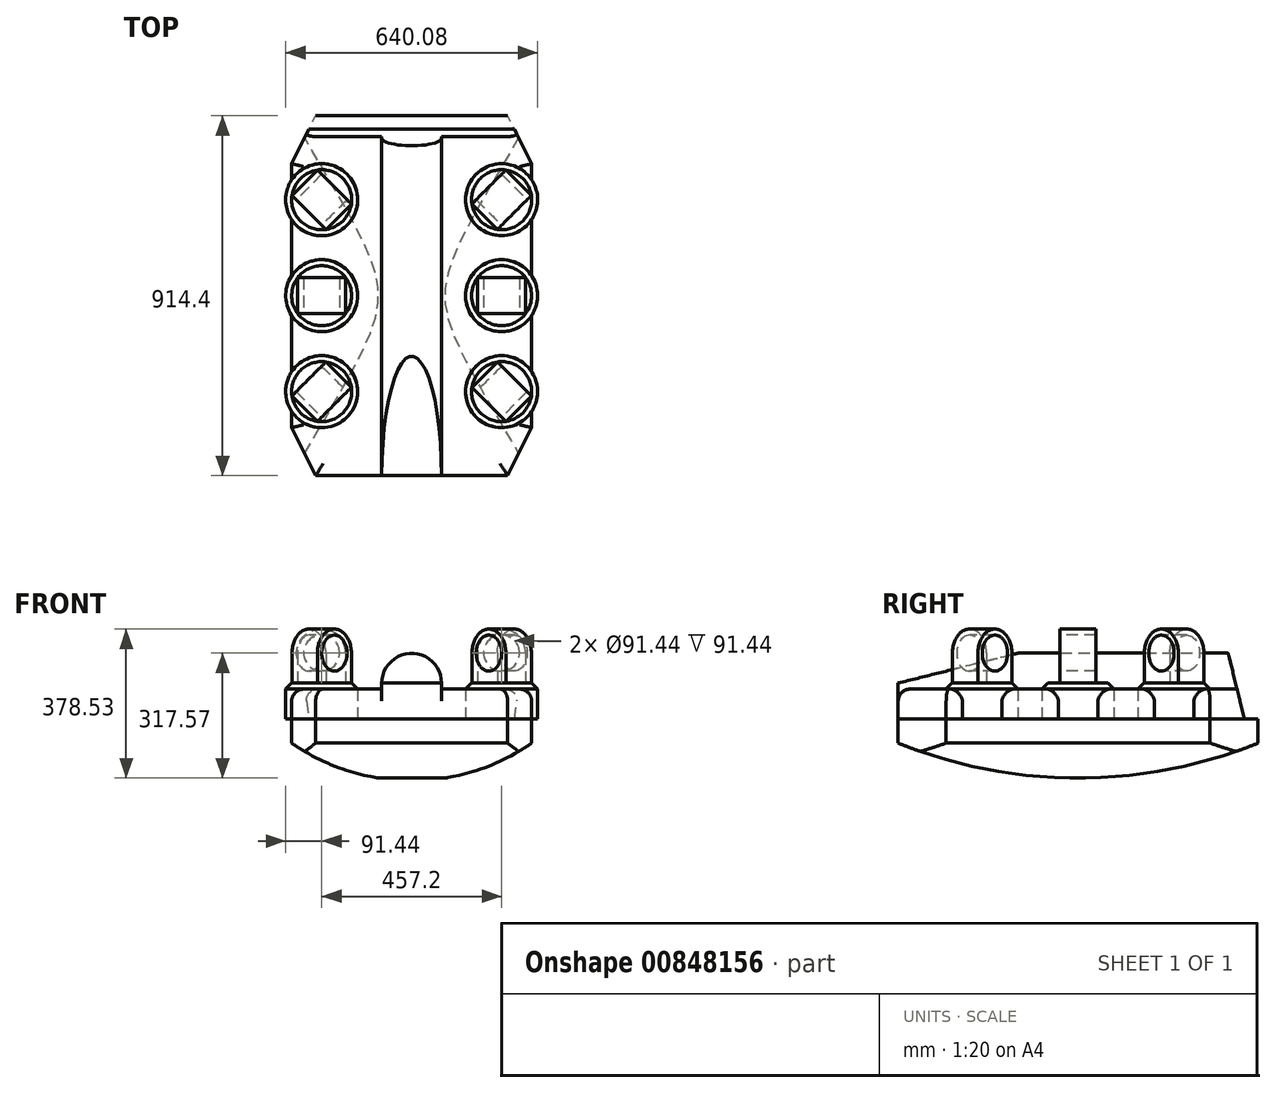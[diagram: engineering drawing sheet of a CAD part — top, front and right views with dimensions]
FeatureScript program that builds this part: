
annotation { "Feature Type Name" : "Feature", "Feature Type Description" : "" }
export const myFeature = defineFeature(function(context is Context, id is Id, definition is map)
    precondition{}
    {
        {
            var Q0;
            Q0=qCreatedBy(makeId("Right.planeOp"),FACE);
            var sketch = newSketch(context, id + "F0", { "sketchPlane" : qUnion([Q0])});
            skLineSegment(sketch, "E0.bottom", {"start": v(-457.2, -30.48) * mm, "end": v(457.2, -30.48) * mm});
            skLineSegment(sketch, "E0.top", {"start": v(-457.2, 30.48) * mm, "end": v(457.2, 30.48) * mm});
            skLineSegment(sketch, "E0.left", {"start": v(-457.2, -30.48) * mm, "end": v(-457.2, 30.48) * mm});
            skLineSegment(sketch, "E0.right", {"start": v(457.2, -30.48) * mm, "end": v(457.2, 30.48) * mm});
            skPoint(sketch, "E0.middle", {"position": v(0, 0) * mm});
            skArc(sketch, "E1", {"start": v(-457.2, -30.48) * mm, "mid": v(0, -119.45) * mm, "end": v(457.2, -30.48) * mm});
            skSolve(sketch);
        }
        {
            var Q0;
            Q0=makeQuery(id+"F0.imprint","IMPRINT",FACE,{"disambiguationData":[TD([[makeQuery(id+"F0.imprint","IMPRINT",EDGE,{"derivedFrom":sQuery(id+"F0.wireOp",EDGE,"E0.bottom")}),1.0]])]});
            var Q1;
            Q1=makeQuery(id+"F0.imprint","IMPRINT",FACE,{"disambiguationData":[TD([[makeQuery(id+"F0.imprint","IMPRINT",EDGE,{"derivedFrom":sQuery(id+"F0.wireOp",EDGE,"E0.bottom")}),-1.0]])]});
            extrude(context, id + "F1", {"entities" : qUnion([Q0, Q1]), "depth" : 609.6 * mm, "offsetDistance" : 30.48 * mm, "symmetric" : true});
        }
        {
            var Q0;
            Q0=qCreatedBy(makeId("Front.planeOp"),FACE);
            var sketch = newSketch(context, id + "F2", { "sketchPlane" : qUnion([Q0])});
            skLineSegment(sketch, "E2.bottom", {"start": v(-304.8, 30.48) * mm, "end": v(304.8, 30.48) * mm});
            skLineSegment(sketch, "E2.top", {"start": v(-304.8, -30.48) * mm, "end": v(304.8, -30.48) * mm});
            skLineSegment(sketch, "E2.left", {"start": v(-304.8, 30.48) * mm, "end": v(-304.8, -30.48) * mm});
            skLineSegment(sketch, "E2.right", {"start": v(304.8, 30.48) * mm, "end": v(304.8, -30.48) * mm});
            skPoint(sketch, "E2.middle", {"position": v(0, 0) * mm});
            skArc(sketch, "E3", {"start": v(-304.8, -30.48) * mm, "mid": v(0, -126.14) * mm, "end": v(304.8, -30.48) * mm});
            skSolve(sketch);
        }
        {
            var Q0;
            Q0 = qSketchRegion(id + "F2", true);
            extrude(context, id + "F3", {"entities" : qUnion([Q0]), "operationType" : NewBodyOperationType.INTERSECT, "depth" : 914.4 * mm, "offsetDistance" : 30.48 * mm, "symmetric" : true});
        }
        {
            var Q0;
            Q0=makeQuery(id+"F1.opExtrude","CAP_EDGE",EDGE,{"disambiguationData":[OSD([sQuery(id+"F0.wireOp",EDGE,"E0.left")])],"isStart":true});
            var Q1;
            Q1=makeQuery(id+"F1.opExtrude","CAP_EDGE",EDGE,{"disambiguationData":[OSD([sQuery(id+"F0.wireOp",EDGE,"E0.left")])],"isStart":false});
            var Q2;
            Q2=makeQuery(id+"F1.opExtrude","CAP_EDGE",EDGE,{"disambiguationData":[OSD([sQuery(id+"F0.wireOp",EDGE,"E0.right")])],"isStart":false});
            var Q3;
            Q3=makeQuery(id+"F1.opExtrude","CAP_EDGE",EDGE,{"disambiguationData":[OSD([sQuery(id+"F0.wireOp",EDGE,"E0.right")])],"isStart":true});
            chamfer(context, id + "F4", {"entities" : qUnion([Q0, Q1, Q2, Q3]), "chamferType" : ChamferType.TWO_OFFSETS, "width1" : 121.92 * mm, "oppositeDirection" : false, "width2" : 60.96 * mm, "tangentPropagation" : true});
        }
        {
            var Q0;
            Q0=makeQuery(id+"F1.opExtrude","SWEPT_FACE",FACE,{"disambiguationData":[OSD([sQuery(id+"F0.wireOp",EDGE,"E0.top")])]});
            var sketch = newSketch(context, id + "F5", { "sketchPlane" : qUnion([Q0])});
            skLineSegment(sketch, "E4.bottom", {"start": v(-228.6, 335.28) * mm, "end": v(228.6, 335.28) * mm});
            skLineSegment(sketch, "E4.top", {"start": v(-228.6, -335.28) * mm, "end": v(228.6, -335.28) * mm});
            skLineSegment(sketch, "E4.left", {"start": v(-228.6, 335.28) * mm, "end": v(-228.6, -335.28) * mm});
            skLineSegment(sketch, "E4.right", {"start": v(228.6, 335.28) * mm, "end": v(228.6, -335.28) * mm});
            skPoint(sketch, "E4.middle", {"position": v(0, 0) * mm});
            skLineSegment(sketch, "E5", {"start": v(-228.6, 243.84) * mm, "end": v(228.6, 243.84) * mm});
            skLineSegment(sketch, "E6", {"start": v(-228.6, 0) * mm, "end": v(228.6, 0) * mm});
            skLineSegment(sketch, "E7", {"start": v(-228.6, -243.84) * mm, "end": v(228.6, -243.84) * mm});
            skCircle(sketch, "E8", {"center": v(-228.6, 243.84) * mm, "radius": 91.44 * mm});
            skCircle(sketch, "E9", {"center": v(-228.6, 0) * mm, "radius": 91.44 * mm});
            skCircle(sketch, "E10", {"center": v(-228.6, -243.84) * mm, "radius": 91.44 * mm});
            skCircle(sketch, "E11", {"center": v(228.6, 243.84) * mm, "radius": 91.44 * mm});
            skCircle(sketch, "E12", {"center": v(228.6, 0) * mm, "radius": 91.44 * mm});
            skCircle(sketch, "E13", {"center": v(228.6, -243.84) * mm, "radius": 91.44 * mm});
            skSolve(sketch);
        }
        {
            var Q0;
            {var subQ1=sQuery(id+"F5.wireOp",EDGE,"E4.left");var subQ7=makeQuery(id+"F5.imprint","INTERSECT",VERTEX,{"derivedFrom":[subQ1,sQuery(id+"F5.wireOp",EDGE,"E5")]});Q0=makeQuery(id+"F5.imprint","IMPRINT",FACE,{"disambiguationData":[TD([[makeQuery(id+"F5.imprint","IMPRINT",EDGE,{"disambiguationData":[TD([[subQ7,-1.0]])],"derivedFrom":subQ1}),-1.0]])]});}
            var Q1;
            {var subQ0=sQuery(id+"F5.wireOp",EDGE,"E5");var subQ1=sQuery(id+"F5.wireOp",EDGE,"E4.left");var subQ2=makeQuery(id+"F5.imprint","INTERSECT",VERTEX,{"derivedFrom":[subQ1,subQ0]});Q1=makeQuery(id+"F5.imprint","IMPRINT",FACE,{"disambiguationData":[TD([[makeQuery(id+"F5.imprint","IMPRINT",EDGE,{"disambiguationData":[TD([[subQ2,-1.0]])],"derivedFrom":subQ1}),1.0]])]});}
            var Q2;
            {var subQ1=sQuery(id+"F5.wireOp",EDGE,"E4.left");var subQ3=sQuery(id+"F5.wireOp",EDGE,"E5");var subQ4=makeQuery(id+"F5.imprint","INTERSECT",VERTEX,{"derivedFrom":[subQ1,subQ3]});Q2=makeQuery(id+"F5.imprint","IMPRINT",FACE,{"disambiguationData":[TD([[makeQuery(id+"F5.imprint","IMPRINT",EDGE,{"disambiguationData":[TD([[subQ4,-1.0]])],"derivedFrom":subQ3}),1.0]])]});}
            var Q3;
            {var subQ0=sQuery(id+"F5.wireOp",EDGE,"E5");var subQ1=sQuery(id+"F5.wireOp",EDGE,"E4.right");var subQ2=makeQuery(id+"F5.imprint","INTERSECT",VERTEX,{"derivedFrom":[subQ1,subQ0]});Q3=makeQuery(id+"F5.imprint","IMPRINT",FACE,{"disambiguationData":[TD([[makeQuery(id+"F5.imprint","IMPRINT",EDGE,{"disambiguationData":[TD([[subQ2,-1.0]])],"derivedFrom":subQ1}),-1.0]])]});}
            var Q4;
            {var subQ1=sQuery(id+"F5.wireOp",EDGE,"E4.right");var subQ3=sQuery(id+"F5.wireOp",EDGE,"E5");var subQ4=makeQuery(id+"F5.imprint","INTERSECT",VERTEX,{"derivedFrom":[subQ1,subQ3]});Q4=makeQuery(id+"F5.imprint","IMPRINT",FACE,{"disambiguationData":[TD([[makeQuery(id+"F5.imprint","IMPRINT",EDGE,{"disambiguationData":[TD([[subQ4,1.0]])],"derivedFrom":subQ3}),1.0]])]});}
            var Q5;
            {var subQ1=sQuery(id+"F5.wireOp",EDGE,"E4.right");var subQ5=makeQuery(id+"F5.imprint","INTERSECT",VERTEX,{"derivedFrom":[subQ1,sQuery(id+"F5.wireOp",EDGE,"E5")]});Q5=makeQuery(id+"F5.imprint","IMPRINT",FACE,{"disambiguationData":[TD([[makeQuery(id+"F5.imprint","IMPRINT",EDGE,{"disambiguationData":[TD([[subQ5,-1.0]])],"derivedFrom":subQ1}),1.0]])]});}
            var Q6;
            {var subQ0=sQuery(id+"F5.wireOp",EDGE,"E6");var subQ1=sQuery(id+"F5.wireOp",EDGE,"E4.right");var subQ2=makeQuery(id+"F5.imprint","INTERSECT",VERTEX,{"derivedFrom":[subQ1,subQ0]});Q6=makeQuery(id+"F5.imprint","IMPRINT",FACE,{"disambiguationData":[TD([[makeQuery(id+"F5.imprint","IMPRINT",EDGE,{"disambiguationData":[TD([[subQ2,1.0]])],"derivedFrom":subQ1}),-1.0]])]});}
            var Q7;
            {var subQ0=sQuery(id+"F5.wireOp",EDGE,"E6");var subQ1=sQuery(id+"F5.wireOp",EDGE,"E4.right");var subQ2=makeQuery(id+"F5.imprint","INTERSECT",VERTEX,{"derivedFrom":[subQ1,subQ0]});Q7=makeQuery(id+"F5.imprint","IMPRINT",FACE,{"disambiguationData":[TD([[makeQuery(id+"F5.imprint","IMPRINT",EDGE,{"disambiguationData":[TD([[subQ2,-1.0]])],"derivedFrom":subQ1}),-1.0]])]});}
            var Q8;
            {var subQ1=sQuery(id+"F5.wireOp",EDGE,"E4.right");var subQ7=makeQuery(id+"F5.imprint","INTERSECT",VERTEX,{"derivedFrom":[subQ1,sQuery(id+"F5.wireOp",EDGE,"E6")]});Q8=makeQuery(id+"F5.imprint","IMPRINT",FACE,{"disambiguationData":[TD([[makeQuery(id+"F5.imprint","IMPRINT",EDGE,{"disambiguationData":[TD([[subQ7,1.0]])],"derivedFrom":subQ1}),1.0]])]});}
            var Q9;
            {var subQ1=sQuery(id+"F5.wireOp",EDGE,"E4.left");var subQ5=makeQuery(id+"F5.imprint","INTERSECT",VERTEX,{"derivedFrom":[subQ1,sQuery(id+"F5.wireOp",EDGE,"E6")]});Q9=makeQuery(id+"F5.imprint","IMPRINT",FACE,{"disambiguationData":[TD([[makeQuery(id+"F5.imprint","IMPRINT",EDGE,{"disambiguationData":[TD([[subQ5,1.0]])],"derivedFrom":subQ1}),-1.0]])]});}
            var Q10;
            {var subQ0=sQuery(id+"F5.wireOp",EDGE,"E6");var subQ1=sQuery(id+"F5.wireOp",EDGE,"E4.left");var subQ2=makeQuery(id+"F5.imprint","INTERSECT",VERTEX,{"derivedFrom":[subQ1,subQ0]});Q10=makeQuery(id+"F5.imprint","IMPRINT",FACE,{"disambiguationData":[TD([[makeQuery(id+"F5.imprint","IMPRINT",EDGE,{"disambiguationData":[TD([[subQ2,-1.0]])],"derivedFrom":subQ1}),1.0]])]});}
            var Q11;
            {var subQ0=sQuery(id+"F5.wireOp",EDGE,"E6");var subQ1=sQuery(id+"F5.wireOp",EDGE,"E4.left");var subQ2=makeQuery(id+"F5.imprint","INTERSECT",VERTEX,{"derivedFrom":[subQ1,subQ0]});Q11=makeQuery(id+"F5.imprint","IMPRINT",FACE,{"disambiguationData":[TD([[makeQuery(id+"F5.imprint","IMPRINT",EDGE,{"disambiguationData":[TD([[subQ2,1.0]])],"derivedFrom":subQ1}),1.0]])]});}
            var Q12;
            {var subQ1=sQuery(id+"F5.wireOp",EDGE,"E4.left");var subQ3=sQuery(id+"F5.wireOp",EDGE,"E7");var subQ4=makeQuery(id+"F5.imprint","INTERSECT",VERTEX,{"derivedFrom":[subQ1,subQ3]});Q12=makeQuery(id+"F5.imprint","IMPRINT",FACE,{"disambiguationData":[TD([[makeQuery(id+"F5.imprint","IMPRINT",EDGE,{"disambiguationData":[TD([[subQ4,-1.0]])],"derivedFrom":subQ3}),-1.0]])]});}
            var Q13;
            {var subQ0=sQuery(id+"F5.wireOp",EDGE,"E7");var subQ1=sQuery(id+"F5.wireOp",EDGE,"E4.left");var subQ2=makeQuery(id+"F5.imprint","INTERSECT",VERTEX,{"derivedFrom":[subQ1,subQ0]});Q13=makeQuery(id+"F5.imprint","IMPRINT",FACE,{"disambiguationData":[TD([[makeQuery(id+"F5.imprint","IMPRINT",EDGE,{"disambiguationData":[TD([[subQ2,1.0]])],"derivedFrom":subQ1}),1.0]])]});}
            var Q14;
            {var subQ1=sQuery(id+"F5.wireOp",EDGE,"E4.left");var subQ5=makeQuery(id+"F5.imprint","INTERSECT",VERTEX,{"derivedFrom":[subQ1,sQuery(id+"F5.wireOp",EDGE,"E7")]});Q14=makeQuery(id+"F5.imprint","IMPRINT",FACE,{"disambiguationData":[TD([[makeQuery(id+"F5.imprint","IMPRINT",EDGE,{"disambiguationData":[TD([[subQ5,1.0]])],"derivedFrom":subQ1}),-1.0]])]});}
            var Q15;
            {var subQ1=sQuery(id+"F5.wireOp",EDGE,"E4.right");var subQ3=sQuery(id+"F5.wireOp",EDGE,"E7");var subQ4=makeQuery(id+"F5.imprint","INTERSECT",VERTEX,{"derivedFrom":[subQ1,subQ3]});Q15=makeQuery(id+"F5.imprint","IMPRINT",FACE,{"disambiguationData":[TD([[makeQuery(id+"F5.imprint","IMPRINT",EDGE,{"disambiguationData":[TD([[subQ4,1.0]])],"derivedFrom":subQ3}),-1.0]])]});}
            var Q16;
            {var subQ0=sQuery(id+"F5.wireOp",EDGE,"E7");var subQ1=sQuery(id+"F5.wireOp",EDGE,"E4.right");var subQ2=makeQuery(id+"F5.imprint","INTERSECT",VERTEX,{"derivedFrom":[subQ1,subQ0]});Q16=makeQuery(id+"F5.imprint","IMPRINT",FACE,{"disambiguationData":[TD([[makeQuery(id+"F5.imprint","IMPRINT",EDGE,{"disambiguationData":[TD([[subQ2,1.0]])],"derivedFrom":subQ1}),-1.0]])]});}
            var Q17;
            {var subQ1=sQuery(id+"F5.wireOp",EDGE,"E4.right");var subQ7=makeQuery(id+"F5.imprint","INTERSECT",VERTEX,{"derivedFrom":[subQ1,sQuery(id+"F5.wireOp",EDGE,"E7")]});Q17=makeQuery(id+"F5.imprint","IMPRINT",FACE,{"disambiguationData":[TD([[makeQuery(id+"F5.imprint","IMPRINT",EDGE,{"disambiguationData":[TD([[subQ7,1.0]])],"derivedFrom":subQ1}),1.0]])]});}
            var Q18;
            {var subQ0=sQuery(id+"F5.wireOp",EDGE,"E13");var subQ1=makeQuery(id+"F1.opExtrude","CAP_EDGE",EDGE,{"disambiguationData":[OSD([sQuery(id+"F0.wireOp",EDGE,"E0.top")])],"isStart":false});var subQ2=makeQuery(id+"F5.imprint","INTERSECT",VERTEX,{"disambiguationData":[OD(0.0)],"derivedFrom":[subQ1,subQ0]});Q18=makeQuery(id+"F5.imprint","IMPRINT",FACE,{"disambiguationData":[TD([[makeQuery(id+"F5.imprint","IMPRINT",EDGE,{"disambiguationData":[TD([[subQ2,1.0]])],"derivedFrom":subQ0}),1.0]])]});}
            var Q19;
            {var subQ0=sQuery(id+"F5.wireOp",EDGE,"E12");var subQ1=makeQuery(id+"F1.opExtrude","CAP_EDGE",EDGE,{"disambiguationData":[OSD([sQuery(id+"F0.wireOp",EDGE,"E0.top")])],"isStart":false});var subQ2=makeQuery(id+"F5.imprint","INTERSECT",VERTEX,{"disambiguationData":[OD(0.0)],"derivedFrom":[subQ1,subQ0]});Q19=makeQuery(id+"F5.imprint","IMPRINT",FACE,{"disambiguationData":[TD([[makeQuery(id+"F5.imprint","IMPRINT",EDGE,{"disambiguationData":[TD([[subQ2,1.0]])],"derivedFrom":subQ0}),1.0]])]});}
            var Q20;
            {var subQ0=sQuery(id+"F5.wireOp",EDGE,"E11");var subQ1=makeQuery(id+"F1.opExtrude","CAP_EDGE",EDGE,{"disambiguationData":[OSD([sQuery(id+"F0.wireOp",EDGE,"E0.top")])],"isStart":false});var subQ2=makeQuery(id+"F5.imprint","INTERSECT",VERTEX,{"disambiguationData":[OD(0.0)],"derivedFrom":[subQ1,subQ0]});Q20=makeQuery(id+"F5.imprint","IMPRINT",FACE,{"disambiguationData":[TD([[makeQuery(id+"F5.imprint","IMPRINT",EDGE,{"disambiguationData":[TD([[subQ2,1.0]])],"derivedFrom":subQ0}),1.0]])]});}
            var Q21;
            {var subQ0=sQuery(id+"F5.wireOp",EDGE,"E8");var subQ1=makeQuery(id+"F1.opExtrude","CAP_EDGE",EDGE,{"disambiguationData":[OSD([sQuery(id+"F0.wireOp",EDGE,"E0.top")])],"isStart":true});var subQ2=makeQuery(id+"F5.imprint","INTERSECT",VERTEX,{"disambiguationData":[OD(0.0)],"derivedFrom":[subQ1,subQ0]});Q21=makeQuery(id+"F5.imprint","IMPRINT",FACE,{"disambiguationData":[TD([[makeQuery(id+"F5.imprint","IMPRINT",EDGE,{"disambiguationData":[TD([[subQ2,-1.0]])],"derivedFrom":subQ0}),1.0]])]});}
            var Q22;
            {var subQ0=sQuery(id+"F5.wireOp",EDGE,"E9");var subQ1=makeQuery(id+"F1.opExtrude","CAP_EDGE",EDGE,{"disambiguationData":[OSD([sQuery(id+"F0.wireOp",EDGE,"E0.top")])],"isStart":true});var subQ2=makeQuery(id+"F5.imprint","INTERSECT",VERTEX,{"disambiguationData":[OD(0.0)],"derivedFrom":[subQ1,subQ0]});Q22=makeQuery(id+"F5.imprint","IMPRINT",FACE,{"disambiguationData":[TD([[makeQuery(id+"F5.imprint","IMPRINT",EDGE,{"disambiguationData":[TD([[subQ2,-1.0]])],"derivedFrom":subQ0}),1.0]])]});}
            var Q23;
            {var subQ0=sQuery(id+"F5.wireOp",EDGE,"E10");var subQ1=makeQuery(id+"F1.opExtrude","CAP_EDGE",EDGE,{"disambiguationData":[OSD([sQuery(id+"F0.wireOp",EDGE,"E0.top")])],"isStart":true});var subQ2=makeQuery(id+"F5.imprint","INTERSECT",VERTEX,{"disambiguationData":[OD(0.0)],"derivedFrom":[subQ1,subQ0]});Q23=makeQuery(id+"F5.imprint","IMPRINT",FACE,{"disambiguationData":[TD([[makeQuery(id+"F5.imprint","IMPRINT",EDGE,{"disambiguationData":[TD([[subQ2,-1.0]])],"derivedFrom":subQ0}),1.0]])]});}
            extrude(context, id + "F6", {"entities" : qUnion([Q0, Q1, Q2, Q3, Q4, Q5, Q6, Q7, Q8, Q9, Q10, Q11, Q12, Q13, Q14, Q15, Q16, Q17, Q18, Q19, Q20, Q21, Q22, Q23]), "operationType" : NewBodyOperationType.ADD, "depth" : 91.44 * mm, "offsetDistance" : 30.48 * mm});
        }
        {
            var Q0;
            Q0=makeQuery(id+"F6.opExtrude","CAP_EDGE",EDGE,{"disambiguationData":[OSD([sQuery(id+"F5.wireOp",EDGE,"E8")])],"isStart":false});
            var Q1;
            Q1=makeQuery(id+"F6.opExtrude","CAP_FACE",FACE,{"disambiguationData":[OSD([sQuery(id+"F5.wireOp",EDGE,"E9")])],"isStart":false});
            var Q2;
            Q2=makeQuery(id+"F6.opExtrude","CAP_FACE",FACE,{"disambiguationData":[OSD([sQuery(id+"F5.wireOp",EDGE,"E10")])],"isStart":false});
            var Q3;
            Q3=makeQuery(id+"F6.opExtrude","CAP_FACE",FACE,{"disambiguationData":[OSD([sQuery(id+"F5.wireOp",EDGE,"E11")])],"isStart":false});
            var Q4;
            Q4=makeQuery(id+"F6.opExtrude","CAP_FACE",FACE,{"disambiguationData":[OSD([sQuery(id+"F5.wireOp",EDGE,"E12")])],"isStart":false});
            var Q5;
            Q5=makeQuery(id+"F6.opExtrude","CAP_FACE",FACE,{"disambiguationData":[OSD([sQuery(id+"F5.wireOp",EDGE,"E13")])],"isStart":false});
            chamfer(context, id + "F7", {"entities" : qUnion([Q0, Q1, Q2, Q3, Q4, Q5]), "width" : 15.24 * mm, "tangentPropagation" : true});
        }
        {
            var Q0;
            Q0=makeQuery(id+"F6.opExtrude","CAP_FACE",FACE,{"disambiguationData":[OSD([sQuery(id+"F5.wireOp",EDGE,"E8")])],"isStart":false});
            var sketch = newSketch(context, id + "F8", { "sketchPlane" : qUnion([Q0])});
            skLineSegment(sketch, "E14.bottom", {"start": v(-250.15, 330.05) * mm, "end": v(-142.39, 222.29) * mm});
            skLineSegment(sketch, "E14.top", {"start": v(-314.81, 265.4) * mm, "end": v(-207.05, 157.63) * mm});
            skLineSegment(sketch, "E14.left", {"start": v(-250.15, 330.05) * mm, "end": v(-314.81, 265.4) * mm});
            skLineSegment(sketch, "E14.right", {"start": v(-142.39, 222.29) * mm, "end": v(-207.05, 157.63) * mm});
            skPoint(sketch, "E14.middle", {"position": v(-228.6, 243.84) * mm});
            skSolve(sketch);
        }
        {
            var Q0;
            {var subQ0=sQuery(id+"F8.wireOp",EDGE,"E14.bottom");var subQ1=sQuery(id+"F5.wireOp",EDGE,"E8");var subQ2=makeQuery(id+"F7.opChamfer","BLEND_EDGE",EDGE,{"blendedFrom":[makeQuery(id+"F6.opExtrude","CAP_EDGE",EDGE,{"disambiguationData":[OSD([subQ1])],"isStart":false}),makeQuery(id+"F6.opExtrude","CAP_FACE",FACE,{"disambiguationData":[OSD([subQ1])],"isStart":false})],"blendedInto":[makeQuery(id+"F6.opExtrude","CAP_FACE",FACE,{"disambiguationData":[OSD([subQ1])],"isStart":false})]});var subQ5=makeQuery(id+"F8.imprint","INTERSECT",VERTEX,{"disambiguationData":[OD(0.0)],"derivedFrom":[subQ2,subQ0]});Q0=makeQuery(id+"F8.imprint","IMPRINT",FACE,{"disambiguationData":[TD([[makeQuery(id+"F8.imprint","IMPRINT",EDGE,{"disambiguationData":[TD([[subQ5,-1.0]])],"derivedFrom":subQ0}),-1.0]])]});}
            extrude(context, id + "F9", {"entities" : qUnion([Q0]), "operationType" : NewBodyOperationType.ADD, "depth" : 152.4 * mm, "offsetDistance" : 30.48 * mm});
        }
        {
            var Q0;
            Q0=makeQuery(id+"F9.opExtrude","SWEPT_FACE",FACE,{"disambiguationData":[OSD([sQuery(id+"F8.wireOp",EDGE,"E14.top")])]});
            var sketch = newSketch(context, id + "F10", { "sketchPlane" : qUnion([Q0])});
            skCircle(sketch, "E15", {"center": v(-334.07, 198.12) * mm, "radius": 45.72 * mm});
            skPoint(sketch, "E15.centerSnap0", {"position": v(-334.07, 274.32) * mm});
            skPoint(sketch, "E15.centerSnap1", {"position": v(-273.1, 198.12) * mm});
            skCircle(sketch, "E16", {"center": v(-334.07, 198.12) * mm, "radius": 60.96 * mm});
            skLineSegment(sketch, "E17.bottom", {"start": v(-410.27, 274.32) * mm, "end": v(-257.87, 274.32) * mm});
            skLineSegment(sketch, "E17.top", {"start": v(-410.27, 121.92) * mm, "end": v(-257.87, 121.92) * mm});
            skLineSegment(sketch, "E17.left", {"start": v(-410.27, 274.32) * mm, "end": v(-410.27, 121.92) * mm});
            skLineSegment(sketch, "E17.right", {"start": v(-257.87, 274.32) * mm, "end": v(-257.87, 121.92) * mm});
            skLineSegment(sketch, "E18", {"start": v(-395.03, 198.12) * mm, "end": v(-395.03, 121.92) * mm});
            skLineSegment(sketch, "E19", {"start": v(-273.1, 198.12) * mm, "end": v(-273.1, 121.92) * mm});
            skSolve(sketch);
        }
        {
            var Q0;
            {var subQ0=sQuery(id+"F10.wireOp",EDGE,"E17.left");Q0=makeQuery(id+"F10.imprint","IMPRINT",FACE,{"disambiguationData":[TD([[makeQuery(id+"F10.imprint","IMPRINT",EDGE,{"derivedFrom":subQ0}),1.0]])]});}
            var Q1;
            {var subQ2=sQuery(id+"F10.wireOp",EDGE,"E17.right");Q1=makeQuery(id+"F10.imprint","IMPRINT",FACE,{"disambiguationData":[TD([[makeQuery(id+"F10.imprint","IMPRINT",EDGE,{"derivedFrom":subQ2}),-1.0]])]});}
            var Q2;
            {var subQ1=sQuery(id+"F8.wireOp",EDGE,"E14.top");var subQ2=sQuery(id+"F5.wireOp",EDGE,"E8");var subQ3=makeQuery(id+"F7.opChamfer","BLEND_EDGE",EDGE,{"blendedFrom":[makeQuery(id+"F6.opExtrude","CAP_EDGE",EDGE,{"disambiguationData":[OSD([subQ2])],"isStart":false}),makeQuery(id+"F6.opExtrude","CAP_FACE",FACE,{"disambiguationData":[OSD([subQ2])],"isStart":false})],"blendedInto":[makeQuery(id+"F6.opExtrude","CAP_FACE",FACE,{"disambiguationData":[OSD([subQ2])],"isStart":false})]});var subQ4=makeQuery(id+"F9.opExtrude","SWEPT_EDGE",EDGE,{"disambiguationData":[OSD([subQ2,subQ1]),TDD([makeQuery(id+"F8.imprint","INTERSECT",VERTEX,{"disambiguationData":[OD(0.0)],"derivedFrom":[subQ3,subQ1]})])]});var subQ8=sQuery(id+"F10.wireOp",EDGE,"E17.bottom");var subQ9=makeQuery(id+"F10.imprint","INTERSECT",VERTEX,{"derivedFrom":[subQ4,subQ8]});Q2=makeQuery(id+"F10.imprint","IMPRINT",FACE,{"disambiguationData":[TD([[makeQuery(id+"F10.imprint","IMPRINT",EDGE,{"disambiguationData":[TD([[subQ9,-1.0]])],"derivedFrom":subQ8}),-1.0]])]});}
            var Q3;
            Q3=makeQuery(id+"F10.imprint","IMPRINT",FACE,{"disambiguationData":[TD([[makeQuery(id+"F10.imprint","IMPRINT",EDGE,{"derivedFrom":sQuery(id+"F10.wireOp",EDGE,"E15")}),1.0]])]});
            extrude(context, id + "F11", {"entities" : qUnion([Q0, Q1, Q2, Q3]), "operationType" : NewBodyOperationType.REMOVE, "oppositeDirection" : true, "depth" : 91.44 * mm, "offsetDistance" : 30.48 * mm});
        }
        {
            var Q0;
            Q0=makeQuery(id+"F6.opExtrude","CAP_FACE",FACE,{"disambiguationData":[OSD([sQuery(id+"F5.wireOp",EDGE,"E9")])],"isStart":false});
            var sketch = newSketch(context, id + "F12", { "sketchPlane" : qUnion([Q0])});
            skLineSegment(sketch, "E20.bottom", {"start": v(-304.8, 45.72) * mm, "end": v(-152.4, 45.72) * mm});
            skLineSegment(sketch, "E20.top", {"start": v(-304.8, -45.72) * mm, "end": v(-152.4, -45.72) * mm});
            skLineSegment(sketch, "E20.left", {"start": v(-304.8, 45.72) * mm, "end": v(-304.8, -45.72) * mm});
            skLineSegment(sketch, "E20.right", {"start": v(-152.4, 45.72) * mm, "end": v(-152.4, -45.72) * mm});
            skPoint(sketch, "E20.middle", {"position": v(-228.6, 0) * mm});
            skSolve(sketch);
        }
        {
            var Q0;
            {var subQ0=sQuery(id+"F12.wireOp",EDGE,"E20.bottom");var subQ1=sQuery(id+"F5.wireOp",EDGE,"E9");var subQ2=makeQuery(id+"F7.opChamfer","BLEND_EDGE",EDGE,{"blendedFrom":[makeQuery(id+"F6.opExtrude","CAP_EDGE",EDGE,{"disambiguationData":[OSD([subQ1])],"isStart":false}),makeQuery(id+"F6.opExtrude","CAP_FACE",FACE,{"disambiguationData":[OSD([subQ1])],"isStart":false})],"blendedInto":[makeQuery(id+"F6.opExtrude","CAP_FACE",FACE,{"disambiguationData":[OSD([subQ1])],"isStart":false})]});var subQ5=makeQuery(id+"F12.imprint","INTERSECT",VERTEX,{"disambiguationData":[OD(0.0)],"derivedFrom":[subQ2,subQ0]});Q0=makeQuery(id+"F12.imprint","IMPRINT",FACE,{"disambiguationData":[TD([[makeQuery(id+"F12.imprint","IMPRINT",EDGE,{"disambiguationData":[TD([[subQ5,-1.0]])],"derivedFrom":subQ0}),-1.0]])]});}
            extrude(context, id + "F13", {"entities" : qUnion([Q0]), "operationType" : NewBodyOperationType.ADD, "depth" : 152.4 * mm, "offsetDistance" : 30.48 * mm});
        }
        {
            var Q0;
            Q0=makeQuery(id+"F13.opExtrude","SWEPT_FACE",FACE,{"disambiguationData":[OSD([sQuery(id+"F12.wireOp",EDGE,"E20.top")])]});
            var sketch = newSketch(context, id + "F14", { "sketchPlane" : qUnion([Q0])});
            skCircle(sketch, "E21", {"center": v(-228.6, 198.12) * mm, "radius": 45.72 * mm});
            skPoint(sketch, "E21.centerSnap0", {"position": v(-228.6, 274.32) * mm});
            skPoint(sketch, "E21.centerSnap1", {"position": v(-167.64, 198.12) * mm});
            skCircle(sketch, "E22", {"center": v(-228.6, 198.12) * mm, "radius": 60.96 * mm});
            skLineSegment(sketch, "E23.bottom", {"start": v(-304.8, 274.32) * mm, "end": v(-152.4, 274.32) * mm});
            skLineSegment(sketch, "E23.top", {"start": v(-304.8, 121.92) * mm, "end": v(-152.4, 121.92) * mm});
            skLineSegment(sketch, "E23.left", {"start": v(-304.8, 274.32) * mm, "end": v(-304.8, 121.92) * mm});
            skLineSegment(sketch, "E23.right", {"start": v(-152.4, 274.32) * mm, "end": v(-152.4, 121.92) * mm});
            skLineSegment(sketch, "E24", {"start": v(-289.56, 198.12) * mm, "end": v(-289.56, 121.92) * mm});
            skLineSegment(sketch, "E25", {"start": v(-167.64, 198.12) * mm, "end": v(-167.64, 121.92) * mm});
            skSolve(sketch);
        }
        {
            var Q0;
            {var subQ5=sQuery(id+"F14.wireOp",EDGE,"E25");Q0=makeQuery(id+"F14.imprint","IMPRINT",FACE,{"disambiguationData":[TD([[makeQuery(id+"F14.imprint","IMPRINT",EDGE,{"derivedFrom":subQ5}),1.0]])]});}
            var Q1;
            {var subQ0=sQuery(id+"F14.wireOp",EDGE,"E23.left");Q1=makeQuery(id+"F14.imprint","IMPRINT",FACE,{"disambiguationData":[TD([[makeQuery(id+"F14.imprint","IMPRINT",EDGE,{"derivedFrom":subQ0}),1.0]])]});}
            var Q2;
            {var subQ4=sQuery(id+"F14.wireOp",EDGE,"E23.right");Q2=makeQuery(id+"F14.imprint","IMPRINT",FACE,{"disambiguationData":[TD([[makeQuery(id+"F14.imprint","IMPRINT",EDGE,{"derivedFrom":subQ4}),-1.0]])]});}
            var Q3;
            Q3=makeQuery(id+"F14.imprint","IMPRINT",FACE,{"disambiguationData":[TD([[makeQuery(id+"F14.imprint","IMPRINT",EDGE,{"derivedFrom":sQuery(id+"F14.wireOp",EDGE,"E21")}),1.0]])]});
            var Q4;
            {var subQ1=sQuery(id+"F12.wireOp",EDGE,"E20.top");var subQ2=sQuery(id+"F5.wireOp",EDGE,"E9");var subQ3=makeQuery(id+"F7.opChamfer","BLEND_EDGE",EDGE,{"blendedFrom":[makeQuery(id+"F6.opExtrude","CAP_EDGE",EDGE,{"disambiguationData":[OSD([subQ2])],"isStart":false}),makeQuery(id+"F6.opExtrude","CAP_FACE",FACE,{"disambiguationData":[OSD([subQ2])],"isStart":false})],"blendedInto":[makeQuery(id+"F6.opExtrude","CAP_FACE",FACE,{"disambiguationData":[OSD([subQ2])],"isStart":false})]});var subQ4=makeQuery(id+"F13.opExtrude","SWEPT_EDGE",EDGE,{"disambiguationData":[OSD([subQ2,subQ1]),TDD([makeQuery(id+"F12.imprint","INTERSECT",VERTEX,{"disambiguationData":[OD(0.0)],"derivedFrom":[subQ3,subQ1]})])]});var subQ8=sQuery(id+"F14.wireOp",EDGE,"E23.bottom");var subQ9=makeQuery(id+"F14.imprint","INTERSECT",VERTEX,{"derivedFrom":[subQ4,subQ8]});Q4=makeQuery(id+"F14.imprint","IMPRINT",FACE,{"disambiguationData":[TD([[makeQuery(id+"F14.imprint","IMPRINT",EDGE,{"disambiguationData":[TD([[subQ9,-1.0]])],"derivedFrom":subQ8}),-1.0]])]});}
            extrude(context, id + "F15", {"entities" : qUnion([Q0, Q1, Q2, Q3, Q4]), "operationType" : NewBodyOperationType.REMOVE, "oppositeDirection" : true, "depth" : 91.44 * mm, "offsetDistance" : 30.48 * mm});
        }
        {
            var Q0;
            Q0=makeQuery(id+"F6.opExtrude","CAP_FACE",FACE,{"disambiguationData":[OSD([sQuery(id+"F5.wireOp",EDGE,"E10")])],"isStart":false});
            var sketch = newSketch(context, id + "F16", { "sketchPlane" : qUnion([Q0])});
            skLineSegment(sketch, "E26.bottom", {"start": v(-314.81, -265.4) * mm, "end": v(-207.05, -157.63) * mm});
            skLineSegment(sketch, "E26.top", {"start": v(-250.15, -330.05) * mm, "end": v(-142.39, -222.29) * mm});
            skLineSegment(sketch, "E26.left", {"start": v(-314.81, -265.4) * mm, "end": v(-250.15, -330.05) * mm});
            skLineSegment(sketch, "E26.right", {"start": v(-207.05, -157.63) * mm, "end": v(-142.39, -222.29) * mm});
            skPoint(sketch, "E26.middle", {"position": v(-228.6, -243.84) * mm});
            skSolve(sketch);
        }
        {
            var Q0;
            {var subQ0=sQuery(id+"F16.wireOp",EDGE,"E26.bottom");var subQ1=sQuery(id+"F5.wireOp",EDGE,"E10");var subQ2=makeQuery(id+"F7.opChamfer","BLEND_EDGE",EDGE,{"blendedFrom":[makeQuery(id+"F6.opExtrude","CAP_EDGE",EDGE,{"disambiguationData":[OSD([subQ1])],"isStart":false}),makeQuery(id+"F6.opExtrude","CAP_FACE",FACE,{"disambiguationData":[OSD([subQ1])],"isStart":false})],"blendedInto":[makeQuery(id+"F6.opExtrude","CAP_FACE",FACE,{"disambiguationData":[OSD([subQ1])],"isStart":false})]});var subQ5=makeQuery(id+"F16.imprint","INTERSECT",VERTEX,{"disambiguationData":[OD(0.0)],"derivedFrom":[subQ2,subQ0]});Q0=makeQuery(id+"F16.imprint","IMPRINT",FACE,{"disambiguationData":[TD([[makeQuery(id+"F16.imprint","IMPRINT",EDGE,{"disambiguationData":[TD([[subQ5,-1.0]])],"derivedFrom":subQ0}),-1.0]])]});}
            extrude(context, id + "F17", {"entities" : qUnion([Q0]), "operationType" : NewBodyOperationType.ADD, "depth" : 152.4 * mm, "offsetDistance" : 30.48 * mm});
        }
        {
            var Q0;
            Q0=makeQuery(id+"F17.opExtrude","SWEPT_FACE",FACE,{"disambiguationData":[OSD([sQuery(id+"F16.wireOp",EDGE,"E26.top")])]});
            var sketch = newSketch(context, id + "F18", { "sketchPlane" : qUnion([Q0])});
            skCircle(sketch, "E27", {"center": v(-334.07, 198.12) * mm, "radius": 45.72 * mm});
            skPoint(sketch, "E27.centerSnap0", {"position": v(-334.07, 274.32) * mm});
            skPoint(sketch, "E27.centerSnap1", {"position": v(-273.1, 198.12) * mm});
            skCircle(sketch, "E28", {"center": v(-334.07, 198.12) * mm, "radius": 60.96 * mm});
            skLineSegment(sketch, "E29.bottom", {"start": v(-410.27, 274.32) * mm, "end": v(-257.87, 274.32) * mm});
            skLineSegment(sketch, "E29.top", {"start": v(-410.27, 121.92) * mm, "end": v(-257.87, 121.92) * mm});
            skLineSegment(sketch, "E29.left", {"start": v(-410.27, 274.32) * mm, "end": v(-410.27, 121.92) * mm});
            skLineSegment(sketch, "E29.right", {"start": v(-257.87, 274.32) * mm, "end": v(-257.87, 121.92) * mm});
            skLineSegment(sketch, "E30", {"start": v(-395.03, 198.12) * mm, "end": v(-395.03, 121.92) * mm});
            skLineSegment(sketch, "E31", {"start": v(-273.1, 198.12) * mm, "end": v(-273.1, 121.92) * mm});
            skSolve(sketch);
        }
        {
            var Q0;
            {var subQ1=sQuery(id+"F16.wireOp",EDGE,"E26.top");var subQ2=sQuery(id+"F5.wireOp",EDGE,"E10");var subQ3=makeQuery(id+"F7.opChamfer","BLEND_EDGE",EDGE,{"blendedFrom":[makeQuery(id+"F6.opExtrude","CAP_EDGE",EDGE,{"disambiguationData":[OSD([subQ2])],"isStart":false}),makeQuery(id+"F6.opExtrude","CAP_FACE",FACE,{"disambiguationData":[OSD([subQ2])],"isStart":false})],"blendedInto":[makeQuery(id+"F6.opExtrude","CAP_FACE",FACE,{"disambiguationData":[OSD([subQ2])],"isStart":false})]});var subQ4=makeQuery(id+"F17.opExtrude","SWEPT_EDGE",EDGE,{"disambiguationData":[OSD([subQ2,subQ1]),TDD([makeQuery(id+"F16.imprint","INTERSECT",VERTEX,{"disambiguationData":[OD(0.0)],"derivedFrom":[subQ3,subQ1]})])]});var subQ8=sQuery(id+"F18.wireOp",EDGE,"E29.bottom");var subQ9=makeQuery(id+"F18.imprint","INTERSECT",VERTEX,{"derivedFrom":[subQ4,subQ8]});Q0=makeQuery(id+"F18.imprint","IMPRINT",FACE,{"disambiguationData":[TD([[makeQuery(id+"F18.imprint","IMPRINT",EDGE,{"disambiguationData":[TD([[subQ9,-1.0]])],"derivedFrom":subQ8}),-1.0]])]});}
            var Q1;
            {var subQ0=sQuery(id+"F18.wireOp",EDGE,"E29.left");Q1=makeQuery(id+"F18.imprint","IMPRINT",FACE,{"disambiguationData":[TD([[makeQuery(id+"F18.imprint","IMPRINT",EDGE,{"derivedFrom":subQ0}),1.0]])]});}
            var Q2;
            {var subQ2=sQuery(id+"F18.wireOp",EDGE,"E29.right");Q2=makeQuery(id+"F18.imprint","IMPRINT",FACE,{"disambiguationData":[TD([[makeQuery(id+"F18.imprint","IMPRINT",EDGE,{"derivedFrom":subQ2}),-1.0]])]});}
            var Q3;
            Q3=makeQuery(id+"F18.imprint","IMPRINT",FACE,{"disambiguationData":[TD([[makeQuery(id+"F18.imprint","IMPRINT",EDGE,{"derivedFrom":sQuery(id+"F18.wireOp",EDGE,"E27")}),1.0]])]});
            extrude(context, id + "F19", {"entities" : qUnion([Q0, Q1, Q2, Q3]), "operationType" : NewBodyOperationType.REMOVE, "oppositeDirection" : true, "depth" : 91.44 * mm, "offsetDistance" : 30.48 * mm});
        }
        {
            var Q0;
            Q0=makeQuery(id+"F1.opExtrude","SWEPT_BODY",BODY,{"disambiguationData":[OSD([sQuery(id+"F0.wireOp",EDGE,"E0.top"),sQuery(id+"F0.wireOp",EDGE,"E0.left"),sQuery(id+"F0.wireOp",EDGE,"E0.right"),sQuery(id+"F0.wireOp",EDGE,"E1")])]});
            var Q1;
            Q1=qCreatedBy(makeId("Right.planeOp"),FACE);
            mirror(context, id + "F20", {"operationType" : NewBodyOperationType.ADD, "entities" : qUnion([Q0]), "mirrorPlane" : qUnion([Q1])});
        }
        {
            var Q0;
            Q0=makeQuery(id+"F1.opExtrude","SWEPT_FACE",FACE,{"disambiguationData":[OSD([sQuery(id+"F0.wireOp",EDGE,"E0.top")])]});
            extrude(context, id + "F21", {"entities" : qUnion([Q0]), "depth" : 76.2 * mm, "offsetDistance" : 30.48 * mm});
        }
        {
            var Q0;
            Q0=makeQuery(id+"F21.opExtrude","CAP_FACE",FACE,{"disambiguationData":[OSD([sQuery(id+"F0.wireOp",EDGE,"E0.top")])],"isStart":false});
            var sketch = newSketch(context, id + "F22", { "sketchPlane" : qUnion([Q0])});
            skLineSegment(sketch, "E32.bottom", {"start": v(-76.2, -457.2) * mm, "end": v(76.2, -457.2) * mm});
            skLineSegment(sketch, "E32.top", {"start": v(-76.2, 457.2) * mm, "end": v(76.2, 457.2) * mm});
            skLineSegment(sketch, "E32.left", {"start": v(-76.2, -457.2) * mm, "end": v(-76.2, 457.2) * mm});
            skLineSegment(sketch, "E32.right", {"start": v(76.2, -457.2) * mm, "end": v(76.2, 457.2) * mm});
            skPoint(sketch, "E32.middle", {"position": v(0, 0) * mm});
            skLineSegment(sketch, "E33.bottom", {"start": v(-76.2, 152.4) * mm, "end": v(76.2, 152.4) * mm});
            skLineSegment(sketch, "E33.top", {"start": v(-76.2, -152.4) * mm, "end": v(76.2, -152.4) * mm});
            skLineSegment(sketch, "E33.left", {"start": v(-76.2, 152.4) * mm, "end": v(-76.2, -152.4) * mm});
            skLineSegment(sketch, "E33.right", {"start": v(76.2, 152.4) * mm, "end": v(76.2, -152.4) * mm});
            skSolve(sketch);
        }
        {
            var Q0;
            Q0=makeQuery(id+"F22.imprint","IMPRINT",FACE,{"disambiguationData":[TD([[makeQuery(id+"F22.imprint","IMPRINT",EDGE,{"derivedFrom":sQuery(id+"F22.wireOp",EDGE,"E33.bottom")}),-1.0]])]});
            var Q1;
            {var subQ0=sQuery(id+"F22.wireOp",EDGE,"E32.top");Q1=makeQuery(id+"F22.imprint","IMPRINT",FACE,{"disambiguationData":[TD([[makeQuery(id+"F22.imprint","IMPRINT",EDGE,{"derivedFrom":subQ0}),1.0]])]});}
            var Q2;
            {var subQ0=sQuery(id+"F22.wireOp",EDGE,"E32.bottom");Q2=makeQuery(id+"F22.imprint","IMPRINT",FACE,{"disambiguationData":[TD([[makeQuery(id+"F22.imprint","IMPRINT",EDGE,{"derivedFrom":subQ0}),-1.0]])]});}
            extrude(context, id + "F23", {"entities" : qUnion([Q0, Q1, Q2]), "operationType" : NewBodyOperationType.ADD, "depth" : 91.44 * mm, "offsetDistance" : 30.48 * mm});
        }
        {
            var Q0;
            Q0=makeQuery(id+"F23.opExtrude","CAP_EDGE",EDGE,{"disambiguationData":[OSD([sQuery(id+"F22.wireOp",EDGE,"E32.bottom")])],"isStart":false});
            var Q1;
            Q1=makeQuery(id+"F23.opExtrude","CAP_EDGE",EDGE,{"disambiguationData":[OSD([sQuery(id+"F22.wireOp",EDGE,"E32.top")])],"isStart":false});
            chamfer(context, id + "F24", {"entities" : qUnion([Q0, Q1]), "chamferType" : ChamferType.TWO_OFFSETS, "width1" : 76.2 * mm, "oppositeDirection" : false, "width2" : 304.8 * mm, "tangentPropagation" : true});
        }
        {
            var Q0;
            Q0=makeQuery(id+"F23.opExtrude","CAP_EDGE",EDGE,{"disambiguationData":[OSD([sQuery(id+"F22.wireOp",EDGE,"E32.left"),sQuery(id+"F22.wireOp",EDGE,"E33.left")])],"isStart":false});
            var Q1;
            Q1=makeQuery(id+"F23.opExtrude","CAP_EDGE",EDGE,{"disambiguationData":[OSD([sQuery(id+"F22.wireOp",EDGE,"E32.right"),sQuery(id+"F22.wireOp",EDGE,"E33.right")])],"isStart":false});
            fillet(context, id + "F25", {"entities" : qUnion([Q0, Q1]), "radius" : 76.2 * mm, "tangentPropagation" : true, "allowEdgeOverflow" : false});
        }
        {
            var Q0;
            {var subQ0=sQuery(id+"F0.wireOp",EDGE,"E0.top");var subQ1=sQuery(id+"F0.wireOp",EDGE,"E0.right");var subQ2=makeQuery(id+"F1.opExtrude","SWEPT_EDGE",EDGE,{"disambiguationData":[OSD([subQ0,subQ1])]});Q0=makeQuery(id+"F23.boolean.opBoolean","SPLIT",EDGE,{"disambiguationData":[TD([makeQuery(id+"F23.opExtrude","SWEPT_FACE",FACE,{"disambiguationData":[OSD([sQuery(id+"F22.wireOp",EDGE,"E32.right"),sQuery(id+"F22.wireOp",EDGE,"E33.right")])]})])],"derivedFrom":makeQuery(id+"F21.opExtrude","CAP_EDGE",EDGE,{"disambiguationData":[OSD([subQ0,subQ1]),TDD([subQ2])],"isStart":false})});}
            var Q1;
            {var subQ0=sQuery(id+"F0.wireOp",EDGE,"E0.top");var subQ1=sQuery(id+"F0.wireOp",EDGE,"E0.right");Q1=makeQuery(id+"F21.opExtrude","CAP_EDGE",EDGE,{"disambiguationData":[OSD([subQ0,subQ1]),TDD([makeQuery(id+"F4.opChamfer","BLEND_EDGE",EDGE,{"blendedFrom":[makeQuery(id+"F1.opExtrude","CAP_EDGE",EDGE,{"disambiguationData":[OSD([subQ1])],"isStart":false}),makeQuery(id+"F1.opExtrude","SWEPT_FACE",FACE,{"disambiguationData":[OSD([subQ0])]})],"blendedInto":[makeQuery(id+"F1.opExtrude","SWEPT_FACE",FACE,{"disambiguationData":[OSD([subQ0])]})]})])],"isStart":false});}
            var Q2;
            {var subQ0=sQuery(id+"F5.wireOp",EDGE,"E11");var subQ1=sQuery(id+"F0.wireOp",EDGE,"E0.top");var subQ2=makeQuery(id+"F1.opExtrude","CAP_FACE",FACE,{"disambiguationData":[OSD([subQ1,sQuery(id+"F0.wireOp",EDGE,"E0.left"),sQuery(id+"F0.wireOp",EDGE,"E0.right"),sQuery(id+"F0.wireOp",EDGE,"E1")])],"isStart":false});var subQ3=makeQuery(id+"F1.opExtrude","SWEPT_FACE",FACE,{"disambiguationData":[OSD([subQ1])]});var subQ4=sQuery(id+"F5.wireOp",EDGE,"E12");Q2=makeQuery(id+"F21.opExtrude","CAP_EDGE",EDGE,{"disambiguationData":[OSD([subQ1]),TDD([makeQuery(id+"F6.boolean.opBoolean","SPLIT",EDGE,{"disambiguationData":[topologyDisambiguationEdgeConnected([subQ3,subQ2]),TD([subQ3,subQ2,makeQuery(id+"F6.opExtrude","SWEPT_FACE",FACE,{"disambiguationData":[OSD([subQ0])]}),makeQuery(id+"F6.opExtrude","CAP_FACE",FACE,{"disambiguationData":[OSD([subQ0])],"isStart":true}),makeQuery(id+"F6.opExtrude","SWEPT_FACE",FACE,{"disambiguationData":[OSD([subQ4])]}),makeQuery(id+"F6.opExtrude","CAP_FACE",FACE,{"disambiguationData":[OSD([subQ4])],"isStart":true})])],"derivedFrom":makeQuery(id+"F1.opExtrude","CAP_EDGE",EDGE,{"disambiguationData":[OSD([subQ1])],"isStart":false})})])],"isStart":false});}
            var Q3;
            {var subQ0=sQuery(id+"F5.wireOp",EDGE,"E12");var subQ1=sQuery(id+"F0.wireOp",EDGE,"E0.top");var subQ2=makeQuery(id+"F1.opExtrude","CAP_FACE",FACE,{"disambiguationData":[OSD([subQ1,sQuery(id+"F0.wireOp",EDGE,"E0.left"),sQuery(id+"F0.wireOp",EDGE,"E0.right"),sQuery(id+"F0.wireOp",EDGE,"E1")])],"isStart":false});var subQ3=sQuery(id+"F5.wireOp",EDGE,"E13");var subQ4=makeQuery(id+"F1.opExtrude","SWEPT_FACE",FACE,{"disambiguationData":[OSD([subQ1])]});Q3=makeQuery(id+"F21.opExtrude","CAP_EDGE",EDGE,{"disambiguationData":[OSD([subQ1]),TDD([makeQuery(id+"F6.boolean.opBoolean","SPLIT",EDGE,{"disambiguationData":[topologyDisambiguationEdgeConnected([subQ4,subQ2]),TD([subQ4,subQ2,makeQuery(id+"F6.opExtrude","SWEPT_FACE",FACE,{"disambiguationData":[OSD([subQ0])]}),makeQuery(id+"F6.opExtrude","CAP_FACE",FACE,{"disambiguationData":[OSD([subQ0])],"isStart":true}),makeQuery(id+"F6.opExtrude","SWEPT_FACE",FACE,{"disambiguationData":[OSD([subQ3])]}),makeQuery(id+"F6.opExtrude","CAP_FACE",FACE,{"disambiguationData":[OSD([subQ3])],"isStart":true})])],"derivedFrom":makeQuery(id+"F1.opExtrude","CAP_EDGE",EDGE,{"disambiguationData":[OSD([subQ1])],"isStart":false})})])],"isStart":false});}
            var Q4;
            {var subQ0=sQuery(id+"F0.wireOp",EDGE,"E0.top");var subQ1=sQuery(id+"F0.wireOp",EDGE,"E0.left");Q4=makeQuery(id+"F21.opExtrude","CAP_EDGE",EDGE,{"disambiguationData":[OSD([subQ0,subQ1]),TDD([makeQuery(id+"F4.opChamfer","BLEND_EDGE",EDGE,{"blendedFrom":[makeQuery(id+"F1.opExtrude","CAP_EDGE",EDGE,{"disambiguationData":[OSD([subQ1])],"isStart":false}),makeQuery(id+"F1.opExtrude","SWEPT_FACE",FACE,{"disambiguationData":[OSD([subQ0])]})],"blendedInto":[makeQuery(id+"F1.opExtrude","SWEPT_FACE",FACE,{"disambiguationData":[OSD([subQ0])]})]})])],"isStart":false});}
            var Q5;
            {var subQ0=sQuery(id+"F0.wireOp",EDGE,"E0.top");var subQ1=sQuery(id+"F0.wireOp",EDGE,"E0.left");var subQ2=makeQuery(id+"F1.opExtrude","SWEPT_EDGE",EDGE,{"disambiguationData":[OSD([subQ0,subQ1])]});Q5=makeQuery(id+"F23.boolean.opBoolean","SPLIT",EDGE,{"disambiguationData":[TD([makeQuery(id+"F23.opExtrude","SWEPT_FACE",FACE,{"disambiguationData":[OSD([sQuery(id+"F22.wireOp",EDGE,"E32.right"),sQuery(id+"F22.wireOp",EDGE,"E33.right")])]})])],"derivedFrom":makeQuery(id+"F21.opExtrude","CAP_EDGE",EDGE,{"disambiguationData":[OSD([subQ0,subQ1]),TDD([subQ2])],"isStart":false})});}
            var Q6;
            {var subQ0=sQuery(id+"F0.wireOp",EDGE,"E0.top");var subQ1=sQuery(id+"F0.wireOp",EDGE,"E0.right");var subQ2=makeQuery(id+"F1.opExtrude","SWEPT_EDGE",EDGE,{"disambiguationData":[OSD([subQ0,subQ1])]});Q6=makeQuery(id+"F23.boolean.opBoolean","SPLIT",EDGE,{"disambiguationData":[TD([makeQuery(id+"F23.opExtrude","SWEPT_FACE",FACE,{"disambiguationData":[OSD([sQuery(id+"F22.wireOp",EDGE,"E32.left"),sQuery(id+"F22.wireOp",EDGE,"E33.left")])]})])],"derivedFrom":makeQuery(id+"F21.opExtrude","CAP_EDGE",EDGE,{"disambiguationData":[OSD([subQ0,subQ1]),TDD([subQ2])],"isStart":false})});}
            var Q7;
            {var subQ0=sQuery(id+"F0.wireOp",EDGE,"E0.top");var subQ1=sQuery(id+"F0.wireOp",EDGE,"E0.right");Q7=makeQuery(id+"F21.opExtrude","CAP_EDGE",EDGE,{"disambiguationData":[OSD([subQ0,subQ1]),TDD([makeQuery(id+"F4.opChamfer","BLEND_EDGE",EDGE,{"blendedFrom":[makeQuery(id+"F1.opExtrude","CAP_EDGE",EDGE,{"disambiguationData":[OSD([subQ1])],"isStart":true}),makeQuery(id+"F1.opExtrude","SWEPT_FACE",FACE,{"disambiguationData":[OSD([subQ0])]})],"blendedInto":[makeQuery(id+"F1.opExtrude","SWEPT_FACE",FACE,{"disambiguationData":[OSD([subQ0])]})]})])],"isStart":false});}
            var Q8;
            {var subQ0=sQuery(id+"F5.wireOp",EDGE,"E8");var subQ1=sQuery(id+"F0.wireOp",EDGE,"E0.top");var subQ2=makeQuery(id+"F1.opExtrude","CAP_FACE",FACE,{"disambiguationData":[OSD([subQ1,sQuery(id+"F0.wireOp",EDGE,"E0.left"),sQuery(id+"F0.wireOp",EDGE,"E0.right"),sQuery(id+"F0.wireOp",EDGE,"E1")])],"isStart":true});var subQ3=sQuery(id+"F5.wireOp",EDGE,"E9");var subQ4=makeQuery(id+"F1.opExtrude","SWEPT_FACE",FACE,{"disambiguationData":[OSD([subQ1])]});Q8=makeQuery(id+"F21.opExtrude","CAP_EDGE",EDGE,{"disambiguationData":[OSD([subQ1]),TDD([makeQuery(id+"F6.boolean.opBoolean","SPLIT",EDGE,{"disambiguationData":[topologyDisambiguationEdgeConnected([subQ4,subQ2]),TD([subQ4,subQ2,makeQuery(id+"F6.opExtrude","SWEPT_FACE",FACE,{"disambiguationData":[OSD([subQ0])]}),makeQuery(id+"F6.opExtrude","CAP_FACE",FACE,{"disambiguationData":[OSD([subQ0])],"isStart":true}),makeQuery(id+"F6.opExtrude","SWEPT_FACE",FACE,{"disambiguationData":[OSD([subQ3])]}),makeQuery(id+"F6.opExtrude","CAP_FACE",FACE,{"disambiguationData":[OSD([subQ3])],"isStart":true})])],"derivedFrom":makeQuery(id+"F1.opExtrude","CAP_EDGE",EDGE,{"disambiguationData":[OSD([subQ1])],"isStart":true})})])],"isStart":false});}
            var Q9;
            {var subQ0=sQuery(id+"F5.wireOp",EDGE,"E9");var subQ1=sQuery(id+"F0.wireOp",EDGE,"E0.top");var subQ2=makeQuery(id+"F1.opExtrude","CAP_FACE",FACE,{"disambiguationData":[OSD([subQ1,sQuery(id+"F0.wireOp",EDGE,"E0.left"),sQuery(id+"F0.wireOp",EDGE,"E0.right"),sQuery(id+"F0.wireOp",EDGE,"E1")])],"isStart":true});var subQ3=makeQuery(id+"F1.opExtrude","SWEPT_FACE",FACE,{"disambiguationData":[OSD([subQ1])]});var subQ4=sQuery(id+"F5.wireOp",EDGE,"E10");Q9=makeQuery(id+"F21.opExtrude","CAP_EDGE",EDGE,{"disambiguationData":[OSD([subQ1]),TDD([makeQuery(id+"F6.boolean.opBoolean","SPLIT",EDGE,{"disambiguationData":[topologyDisambiguationEdgeConnected([subQ3,subQ2]),TD([subQ3,subQ2,makeQuery(id+"F6.opExtrude","SWEPT_FACE",FACE,{"disambiguationData":[OSD([subQ0])]}),makeQuery(id+"F6.opExtrude","CAP_FACE",FACE,{"disambiguationData":[OSD([subQ0])],"isStart":true}),makeQuery(id+"F6.opExtrude","SWEPT_FACE",FACE,{"disambiguationData":[OSD([subQ4])]}),makeQuery(id+"F6.opExtrude","CAP_FACE",FACE,{"disambiguationData":[OSD([subQ4])],"isStart":true})])],"derivedFrom":makeQuery(id+"F1.opExtrude","CAP_EDGE",EDGE,{"disambiguationData":[OSD([subQ1])],"isStart":true})})])],"isStart":false});}
            var Q10;
            {var subQ0=sQuery(id+"F0.wireOp",EDGE,"E0.top");var subQ1=sQuery(id+"F0.wireOp",EDGE,"E0.left");Q10=makeQuery(id+"F21.opExtrude","CAP_EDGE",EDGE,{"disambiguationData":[OSD([subQ0,subQ1]),TDD([makeQuery(id+"F4.opChamfer","BLEND_EDGE",EDGE,{"blendedFrom":[makeQuery(id+"F1.opExtrude","CAP_EDGE",EDGE,{"disambiguationData":[OSD([subQ1])],"isStart":true}),makeQuery(id+"F1.opExtrude","SWEPT_FACE",FACE,{"disambiguationData":[OSD([subQ0])]})],"blendedInto":[makeQuery(id+"F1.opExtrude","SWEPT_FACE",FACE,{"disambiguationData":[OSD([subQ0])]})]})])],"isStart":false});}
            var Q11;
            {var subQ0=sQuery(id+"F0.wireOp",EDGE,"E0.top");var subQ1=sQuery(id+"F0.wireOp",EDGE,"E0.left");var subQ2=makeQuery(id+"F1.opExtrude","SWEPT_EDGE",EDGE,{"disambiguationData":[OSD([subQ0,subQ1])]});Q11=makeQuery(id+"F23.boolean.opBoolean","SPLIT",EDGE,{"disambiguationData":[TD([makeQuery(id+"F23.opExtrude","SWEPT_FACE",FACE,{"disambiguationData":[OSD([sQuery(id+"F22.wireOp",EDGE,"E32.left"),sQuery(id+"F22.wireOp",EDGE,"E33.left")])]})])],"derivedFrom":makeQuery(id+"F21.opExtrude","CAP_EDGE",EDGE,{"disambiguationData":[OSD([subQ0,subQ1]),TDD([subQ2])],"isStart":false})});}
            fillet(context, id + "F26", {"entities" : qUnion([Q0, Q1, Q2, Q3, Q4, Q5, Q6, Q7, Q8, Q9, Q10, Q11]), "radius" : 30.48 * mm, "tangentPropagation" : true, "allowEdgeOverflow" : false});
        }
    });
